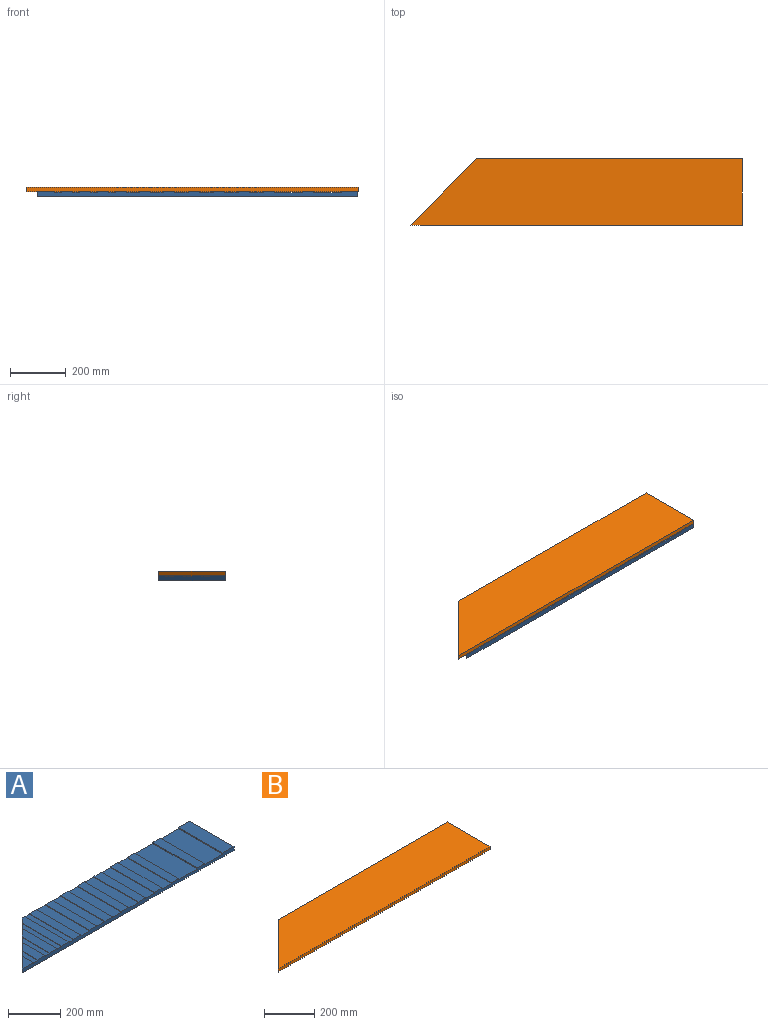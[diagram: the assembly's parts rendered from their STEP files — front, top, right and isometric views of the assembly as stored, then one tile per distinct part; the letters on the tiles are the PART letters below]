
ASSEMBLY  parts=2 mates=1
PART A: 54 faces, bbox 1150x240x18 mm
  f0: plane 240x40mm, normal (0,0,1), area 9287.5mm2, adj f4,f5,f15,f49,f52
  f1: plane 190x40mm, normal (0,0,1), area 6800mm2, adj f4,f5,f46,f48
  f2: plane 125x40mm, normal (0,0,1), area 4200mm2, adj f4,f5,f43,f45
  f3: plane 60x60mm, normal (0,0,1), area 1800mm2, adj f4,f5,f42
  f4: plane 1150x18mm, normal (0,-1,0), area 18630mm2, adj f0,f1,f2,f3,f5,f6,f7,f8
  f5: plane 240x240mm, normal (-0.71,0.71,0), area 5897.3mm2, adj f0,f1,f2,f3,f4,f15,f17,f42
  f6: plane 240x40mm, normal (0,0,1), area 9600mm2, adj f4,f15,f36,f40
  f7: plane 240x40mm, normal (0,0,1), area 9600mm2, adj f4,f15,f33,f37
  f8: plane 240x40mm, normal (0,0,1), area 9600mm2, adj f4,f15,f30,f34
  f9: plane 240x40mm, normal (0,0,1), area 9600mm2, adj f4,f15,f27,f31
  f10: plane 240x40mm, normal (0,0,1), area 9600mm2, adj f4,f15,f25,f28
  f11: plane 240x40mm, normal (0,0,1), area 9600mm2, adj f4,f15,f24,f51
  f12: plane 240x40mm, normal (0,0,1), area 9600mm2, adj f4,f15,f18,f22
  f13: plane 240x40mm, normal (0,0,1), area 9600mm2, adj f4,f15,f19,f39
  f14: plane 240x18mm, normal (1,0,0), area 4320mm2, adj f4,f15,f16,f17
  f15: plane 910x18mm, normal (0,1,0), area 14460mm2, adj f0,f5,f6,f7,f8,f9,f10,f11
  f16: plane 240x60mm, normal (0,0,1), area 14400mm2, adj f4,f14,f15,f21
  f17: plane 1150x240mm, normal (0,0,-1), area 247200mm2, adj f4,f5,f14,f15
  f18: plane 240x5mm, normal (-1,0,0), area 1200mm2, adj f4,f12,f15,f20
  f19: plane 240x5mm, normal (1,0,0), area 1200mm2, adj f4,f13,f15,f20
  f20: plane 240x100mm, normal (0,0,1), area 24000mm2, adj f4,f15,f18,f19
  f21: plane 240x5mm, normal (-1,0,0), area 1200mm2, adj f4,f15,f16,f23
  f22: plane 240x5mm, normal (1,0,0), area 1200mm2, adj f4,f12,f15,f23
  f23: plane 240x100mm, normal (0,0,1), area 24000mm2, adj f4,f15,f21,f22
  f24: plane 240x3mm, normal (1,0,0), area 720mm2, adj f4,f11,f15,f26
  f25: plane 240x3mm, normal (-1,0,0), area 720mm2, adj f4,f10,f15,f26
  f26: plane 240x45mm, normal (0,0,1), area 10800mm2, adj f4,f15,f24,f25
  f27: plane 240x3mm, normal (-1,0,0), area 720mm2, adj f4,f9,f15,f29
  f28: plane 240x3mm, normal (1,0,0), area 720mm2, adj f4,f10,f15,f29
  f29: plane 240x45mm, normal (0,0,1), area 10800mm2, adj f4,f15,f27,f28
  f30: plane 240x3mm, normal (-1,0,0), area 720mm2, adj f4,f8,f15,f32
  f31: plane 240x3mm, normal (1,0,0), area 720mm2, adj f4,f9,f15,f32
  f32: plane 240x50mm, normal (0,0,1), area 12000mm2, adj f4,f15,f30,f31
  f33: plane 240x3mm, normal (-1,0,0), area 720mm2, adj f4,f7,f15,f35
  f34: plane 240x3mm, normal (1,0,0), area 720mm2, adj f4,f8,f15,f35
  f35: plane 240x50mm, normal (0,0,1), area 12000mm2, adj f4,f15,f33,f34
  f36: plane 240x3mm, normal (-1,0,0), area 720mm2, adj f4,f6,f15,f38
  f37: plane 240x3mm, normal (1,0,0), area 720mm2, adj f4,f7,f15,f38
  f38: plane 240x50mm, normal (0,0,1), area 12000mm2, adj f4,f15,f36,f37
  f39: plane 240x3mm, normal (-1,0,0), area 720mm2, adj f4,f13,f15,f41
  f40: plane 240x3mm, normal (1,0,0), area 720mm2, adj f4,f6,f15,f41
  f41: plane 240x50mm, normal (0,0,1), area 12000mm2, adj f4,f15,f39,f40
  f42: plane 60x2mm, normal (1,0,0), area 120mm2, adj f3,f4,f5,f44
  f43: plane 85x2mm, normal (-1,0,0), area 170mm2, adj f2,f4,f5,f44
  f44: plane 85x25mm, normal (0,0,1), area 1812.5mm2, adj f4,f5,f42,f43
  f45: plane 125x2mm, normal (1,0,0), area 250mm2, adj f2,f4,f5,f47
  f46: plane 150x2mm, normal (-1,0,0), area 300mm2, adj f1,f4,f5,f47
  f47: plane 150x25mm, normal (0,0,1), area 3437.5mm2, adj f4,f5,f45,f46
  f48: plane 190x2mm, normal (1,0,0), area 380mm2, adj f1,f4,f5,f50
  f49: plane 215x2mm, normal (-1,0,0), area 430mm2, adj f0,f4,f5,f50
  f50: plane 215x25mm, normal (0,0,1), area 5062.5mm2, adj f4,f5,f48,f49
  f51: plane 240x2mm, normal (-1,0,0), area 480mm2, adj f4,f11,f15,f53
  f52: plane 240x2mm, normal (1,0,0), area 480mm2, adj f0,f4,f15,f53
  f53: plane 240x25mm, normal (0,0,1), area 6000mm2, adj f4,f15,f51,f52
PART B: 6 faces, bbox 1192.4x240x15 mm
  f0: plane 952.43x15mm, normal (0,1,0), area 14286.4mm2, adj f1,f3,f4,f5
  f1: plane 240x240mm, normal (-0.71,0.71,0), area 5091.2mm2, adj f0,f2,f4,f5
  f2: plane 1192.43x15mm, normal (0,-1,0), area 17886.4mm2, adj f1,f3,f4,f5
  f3: plane 240x15mm, normal (1,0,0), area 3600mm2, adj f0,f2,f4,f5
  f4: plane 1192.43x240mm, normal (0,0,1), area 257382.3mm2, adj f0,f1,f2,f3
  f5: plane 1192.43x240mm, normal (0,0,-1), area 257382.3mm2, adj f0,f1,f2,f3
PLACE A at identity
PLACE B t=(-499.97,98.24,18)mm
MATE fastened B.f5 <-> A.f16  axis (0,0,-1) through (0,120,18)mm
